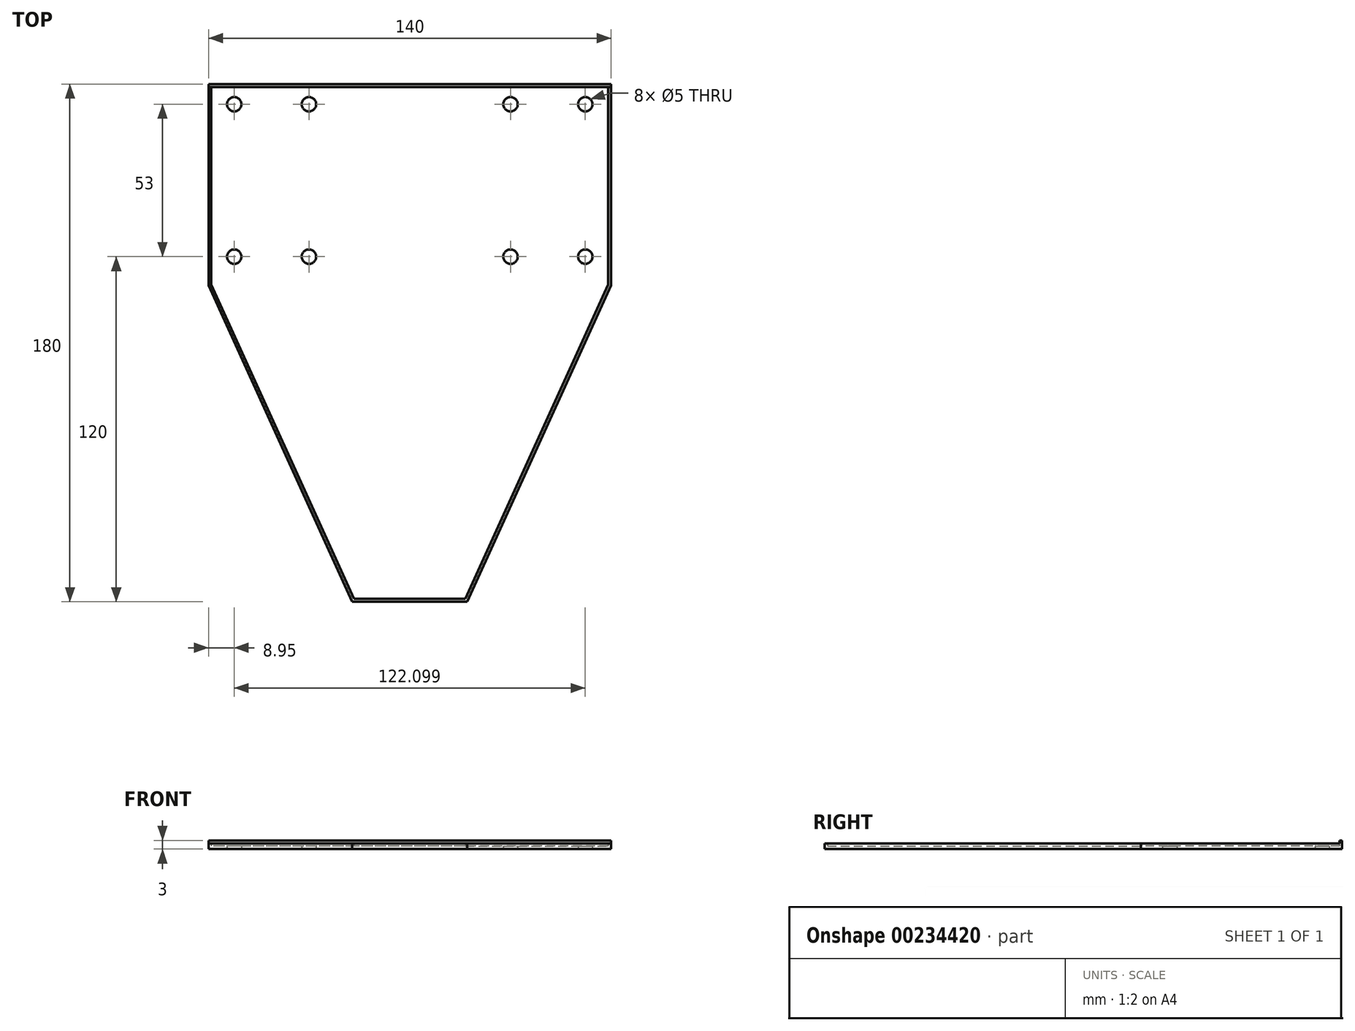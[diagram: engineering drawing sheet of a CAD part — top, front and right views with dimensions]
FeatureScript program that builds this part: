
annotation { "Feature Type Name" : "Feature", "Feature Type Description" : "" }
export const myFeature = defineFeature(function(context is Context, id is Id, definition is map)
    precondition{}
    {
        {
            var Q0;
            Q0=qCreatedBy(makeId("Top.planeOp"),FACE);
            var sketch = newSketch(context, id + "F0", { "sketchPlane" : qUnion([Q0])});
            skLineSegment(sketch, "E0", {"start": v(0, 0) * mm, "end": v(0, 180) * mm});
            skLineSegment(sketch, "E1", {"start": v(0, 180) * mm, "end": v(-70, 180) * mm});
            skLineSegment(sketch, "E2", {"start": v(-70, 180) * mm, "end": v(-70, 110) * mm});
            skLineSegment(sketch, "E3", {"start": v(0, 0) * mm, "end": v(-20, 0) * mm});
            skLineSegment(sketch, "E4", {"start": v(-20, 0) * mm, "end": v(-70, 110) * mm});
            skCircle(sketch, "E5", {"center": v(-61.05, 173) * mm, "radius": 2.5 * mm});
            skLineSegment(sketch, "E6", {"start": v(-61.05, 173) * mm, "end": v(-61.05, 120) * mm});
            skCircle(sketch, "E7", {"center": v(-61.05, 120) * mm, "radius": 2.5 * mm});
            skLineSegment(sketch, "E8", {"start": v(-61.05, 120) * mm, "end": v(-35.05, 120) * mm});
            skLineSegment(sketch, "E9", {"start": v(-35.05, 120) * mm, "end": v(-35.05, 173) * mm});
            skCircle(sketch, "E10", {"center": v(-35.05, 120) * mm, "radius": 2.5 * mm});
            skCircle(sketch, "E11", {"center": v(-35.05, 173) * mm, "radius": 2.5 * mm});
            skSolve(sketch);
        }
        {
            var Q0;
            Q0=makeQuery(id+"F0.imprint","IMPRINT",FACE,{"disambiguationData":[TD([[makeQuery(id+"F0.imprint","IMPRINT",EDGE,{"derivedFrom":sQuery(id+"F0.wireOp",EDGE,"E0")}),1.0]])]});
            extrude(context, id + "F1", {"entities" : qUnion([Q0]), "depth" : 1 * mm});
        }
        {
            var Q0;
            Q0=makeQuery(id+"F1.opExtrude","SWEPT_BODY",BODY,{"disambiguationData":[OSD([sQuery(id+"F0.wireOp",EDGE,"E0"),sQuery(id+"F0.wireOp",EDGE,"E1"),sQuery(id+"F0.wireOp",EDGE,"E2"),sQuery(id+"F0.wireOp",EDGE,"E3"),sQuery(id+"F0.wireOp",EDGE,"E4"),sQuery(id+"F0.wireOp",EDGE,"E5"),sQuery(id+"F0.wireOp",EDGE,"E7"),sQuery(id+"F0.wireOp",EDGE,"E10"),sQuery(id+"F0.wireOp",EDGE,"E11")])]});
            var Q1;
            Q1=makeQuery(id+"F1.opExtrude","SWEPT_FACE",FACE,{"disambiguationData":[OSD([sQuery(id+"F0.wireOp",EDGE,"E0")])]});
            mirror(context, id + "F2", {"operationType" : NewBodyOperationType.ADD, "entities" : qUnion([Q0]), "mirrorPlane" : qUnion([Q1])});
        }
        {
            var Q0;
            {var subQ0=makeQuery(id+"F1.opExtrude","CAP_FACE",FACE,{"disambiguationData":[OSD([sQuery(id+"F0.wireOp",EDGE,"E0"),sQuery(id+"F0.wireOp",EDGE,"E1"),sQuery(id+"F0.wireOp",EDGE,"E2"),sQuery(id+"F0.wireOp",EDGE,"E3"),sQuery(id+"F0.wireOp",EDGE,"E4"),sQuery(id+"F0.wireOp",EDGE,"E5"),sQuery(id+"F0.wireOp",EDGE,"E7"),sQuery(id+"F0.wireOp",EDGE,"E10"),sQuery(id+"F0.wireOp",EDGE,"E11")])],"isStart":false});Q0=makeQuery(id+"F2.boolean.opBoolean","MERGE",FACE,{"derivedFrom":[subQ0,makeQuery(id+"F2.opPattern","COPY",FACE,{"derivedFrom":subQ0,"instanceName":"1"})]});}
            var sketch = newSketch(context, id + "F3", { "sketchPlane" : qUnion([Q0])});
            skLineSegment(sketch, "E12.0", {"start": v(70, 179) * mm, "end": v(-70, 179) * mm});
            skSolve(sketch);
        }
        {
            var Q0;
            Q0=qSketchRegion(id+"F3",true);
            var Q1;
            {var subQ0=sQuery(id+"F3.wireOp",EDGE,"E12.0");Q1=makeQuery(id+"F3.imprint","IMPRINT",FACE,{"disambiguationData":[TD([[makeQuery(id+"F3.imprint","IMPRINT",EDGE,{"derivedFrom":subQ0}),-1.0]])]});}
            extrude(context, id + "F4", {"entities" : qUnion([Q0, Q1]), "operationType" : NewBodyOperationType.ADD, "depth" : 2 * mm});
        }
        {
            var Q0;
            {var subQ0=makeQuery(id+"F1.opExtrude","CAP_FACE",FACE,{"disambiguationData":[OSD([sQuery(id+"F0.wireOp",EDGE,"E0"),sQuery(id+"F0.wireOp",EDGE,"E1"),sQuery(id+"F0.wireOp",EDGE,"E2"),sQuery(id+"F0.wireOp",EDGE,"E3"),sQuery(id+"F0.wireOp",EDGE,"E4"),sQuery(id+"F0.wireOp",EDGE,"E5"),sQuery(id+"F0.wireOp",EDGE,"E7"),sQuery(id+"F0.wireOp",EDGE,"E10"),sQuery(id+"F0.wireOp",EDGE,"E11")])],"isStart":false});Q0=makeQuery(id+"F2.boolean.opBoolean","MERGE",FACE,{"derivedFrom":[subQ0,makeQuery(id+"F2.opPattern","COPY",FACE,{"derivedFrom":subQ0,"instanceName":"1"})]});}
            var sketch = newSketch(context, id + "F5", { "sketchPlane" : qUnion([Q0])});
            skLineSegment(sketch, "E13.0", {"start": v(-69, 179) * mm, "end": v(-69, 110) * mm});
            skLineSegment(sketch, "E14.0", {"start": v(16.78, 5) * mm, "end": v(65, 111.08) * mm});
            skLineSegment(sketch, "E14.1", {"start": v(65, 174) * mm, "end": v(-65, 174) * mm});
            skLineSegment(sketch, "E14.2", {"start": v(-65, 174) * mm, "end": v(-65, 111.08) * mm});
            skLineSegment(sketch, "E14.3", {"start": v(65, 111.08) * mm, "end": v(65, 174) * mm});
            skLineSegment(sketch, "E14.4", {"start": v(-65, 111.08) * mm, "end": v(-16.78, 5) * mm});
            skLineSegment(sketch, "E14.5", {"start": v(-16.78, 5) * mm, "end": v(16.78, 5) * mm});
            skLineSegment(sketch, "E15.0", {"start": v(-19.09, 0.41) * mm, "end": v(-69.09, 110.41) * mm});
            skLineSegment(sketch, "E16.0", {"start": v(69, 179) * mm, "end": v(69, 110) * mm});
            skLineSegment(sketch, "E17.0", {"start": v(19.09, 0.41) * mm, "end": v(69.09, 110.41) * mm});
            skLineSegment(sketch, "E18.0", {"start": v(20, 1) * mm, "end": v(-20, 1) * mm});
            skLineSegment(sketch, "E19.0", {"start": v(-16.78, 0) * mm, "end": v(16.78, 0) * mm});
            skSolve(sketch);
        }
        {
            var Q0;
            {var subQ5=sQuery(id+"F5.wireOp",EDGE,"E19.0");Q0=makeQuery(id+"F5.imprint","IMPRINT",FACE,{"disambiguationData":[TD([[makeQuery(id+"F5.imprint","IMPRINT",EDGE,{"derivedFrom":subQ5}),-1.0]])]});}
            extrude(context, id + "F6", {"entities" : qUnion([Q0]), "operationType" : NewBodyOperationType.ADD, "depth" : 1 * mm});
        }
    });
